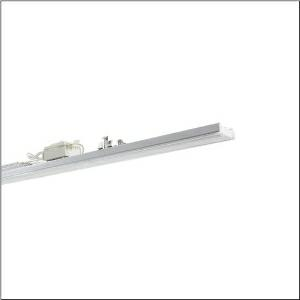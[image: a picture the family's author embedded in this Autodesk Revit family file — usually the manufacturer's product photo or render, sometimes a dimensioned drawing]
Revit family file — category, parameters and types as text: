
# Revit family: licross_11_recessed_mo_51tl12dn49xg
name_source: partatom
category: Lighting Fixtures
units: mm (PartAtom-declared; Revit-internal decimal feet)

## family parameters
Cut with Voids When Loaded = No
Host = Face
Light Source = No
Part Type = Normal
Room Calculation Point = No
Round Connector Dimension = Use Diameter
Shared = No

## types (1)
- --- (1 x LED, 9140 lm, 50.1 W, 4000K)
    Apparent Load = 50 VA
    CIE Flux Codes = 67 92 99 100 100
    Color Rendering = 80
    Color Temperature = 4000K
    Default Elevation = 1800 mm
    Description = Licross 11 Recessed MO, luminaire insert, of sheet steel, coil coated, white, length: 1.500mm, width: 66mm, height: 67mm, LED rated luminous flux: 9.140lm, light colour: 840, SDCM (Standard Deviation of Colour Matching)MacAdam ≤ 2 SDCM (initial), control gear: DALI 2, with plug, 5-pole, with phase selection, mains connection: 220..240V, AC, 50/60Hz, rated input power: 50W, internal wiring halogen-free, primary optical cover: cover, of PMMA, light emission: direct distribution, primary light characteristic: symmetric, protection rating (complete): IP40, insulation class (complete): insulation class I (protective earthing), certification: CE, ENEC, VDE, UKCA, protection symbol: D if used in an environment without relevant dust loads with corresponding accessories, impact resistance: IK06, permissible ambient temperature for indoor applications: -25..+35°C, corresponds to IFS (International Featured Standards) requirements for safety and quality in the food industry, reducing of maximum allowable ambient temperature of 5°C with ceiling mounting, LABS conformity tested according to VDMA 24364:2018-05, The light source and the operating device comply with the requirements of the Ecodesign Regulation (EU) 2019/2020 and are replaceable in accordance with this regulation, packaging unit: 1 piece
    Height = 58 mm
    Lamp = 1 x LED
    Lamp Light Flux = 9140 lm
    Lamp Power = 50.1 W
    Lamp count = 1
    Length = 1500 mm
    Luminous efficacy = 182 lm/W
    Manufacturer = Siteco
    ModVariant = No
    Model = 51TL12DN49XG
    Mounting Place = Ceiling
    Mounting Type = Pendant
    Number of Poles = 1
    OnlyDefault = Yes
    Power Factor = 1
    Product Name = Licross 11 Recessed MO
    Product group = luminaire insert | ceiling pendant
    ProductGroupID = 901
    Protection Class = Protection class I
    Protection Degree = IP 40
    RLX_Detail_Level = 1
    RLX_Emergency_Light_Flux = 0 lm
    RLX_Emergency_Type = 0
    RLX_Emergency_Type_DB = No
    RlxData = <blob elided: 24733 chars, md5=8e8e0615>
    Socket = socket
    Standby Power = 0 W
    System Light Flux = 9140 lm
    System Power = 50 W
    Type Comments = factory setting: luminous flux: 100 % | dim-lin: 254 | 334 mA
    Type Image = l_1296930.jpg
    URL = http://relux.com
    VarID = @adj_029169
    Voltage = 0 V
    Weight = 0.00 kg
    Width = 66 mm

## geometry (parser evidence)
native form markers: Blend x4, Sweep x12
no freeform markers — native parametric forms only
